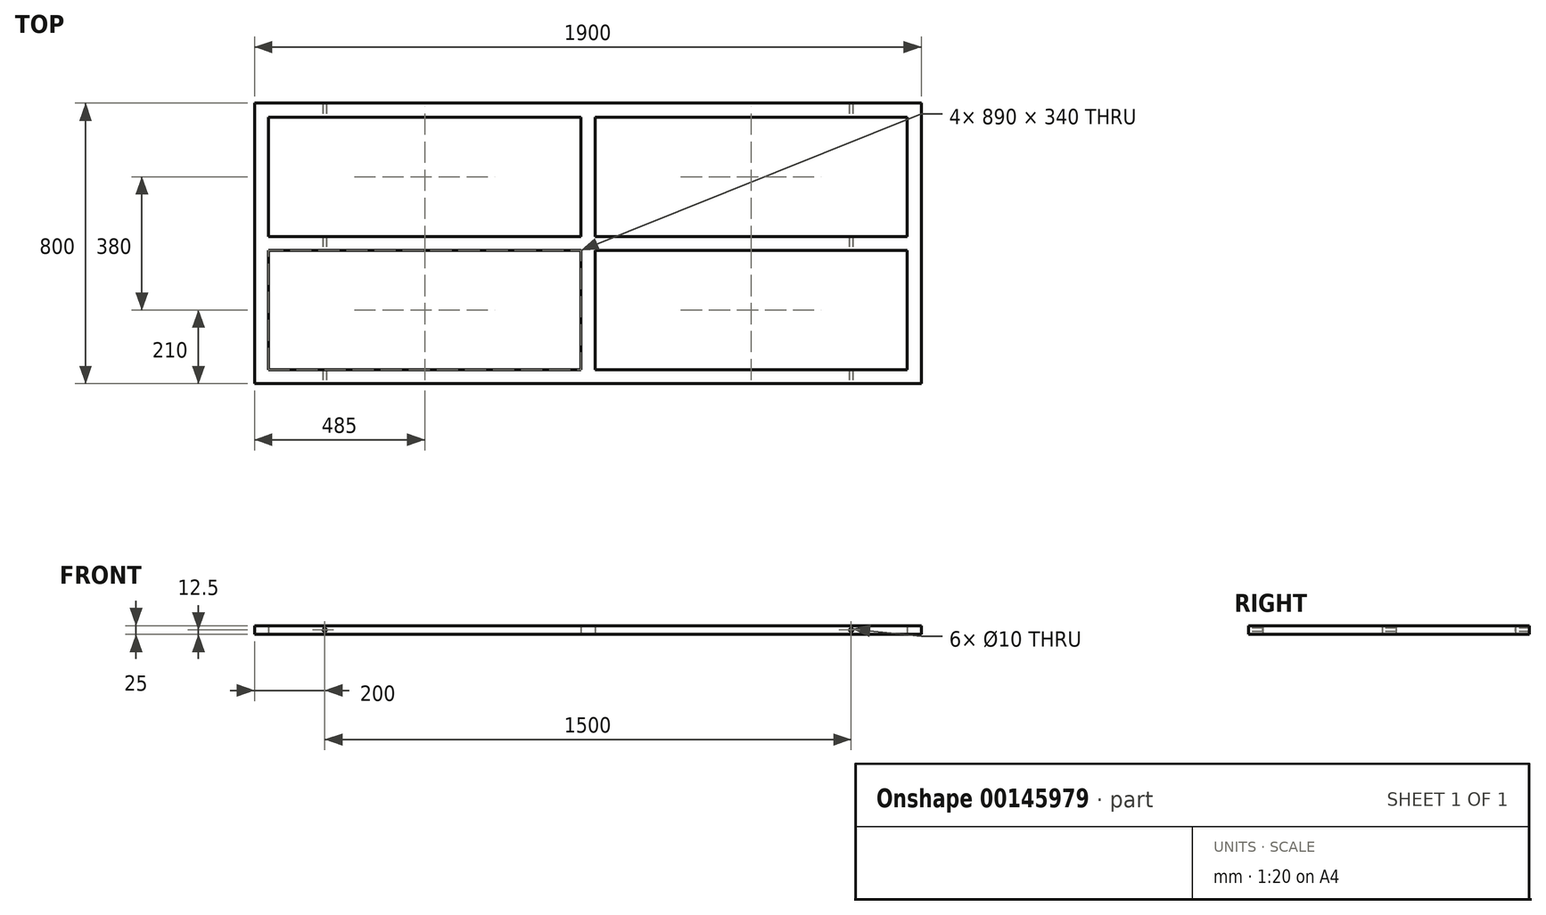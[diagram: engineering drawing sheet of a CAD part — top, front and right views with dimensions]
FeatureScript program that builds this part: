
annotation { "Feature Type Name" : "Feature", "Feature Type Description" : "" }
export const myFeature = defineFeature(function(context is Context, id is Id, definition is map)
    precondition{}
    {
        {
            var Q0;
            Q0=qCreatedBy(makeId("Top.planeOp"),FACE);
            var sketch = newSketch(context, id + "F0", { "sketchPlane" : qUnion([Q0])});
            skLineSegment(sketch, "E0.bottom", {"start": v(950, 400) * mm, "end": v(-950, 400) * mm});
            skLineSegment(sketch, "E0.top", {"start": v(950, -400) * mm, "end": v(-950, -400) * mm});
            skLineSegment(sketch, "E0.left", {"start": v(950, 400) * mm, "end": v(950, -400) * mm});
            skLineSegment(sketch, "E0.right", {"start": v(-950, 400) * mm, "end": v(-950, -400) * mm});
            skPoint(sketch, "E0.middle", {"position": v(0, 0) * mm});
            skLineSegment(sketch, "E1.bottom", {"start": v(910, 360) * mm, "end": v(-910, 360) * mm});
            skLineSegment(sketch, "E1.top", {"start": v(910, -360) * mm, "end": v(-910, -360) * mm});
            skLineSegment(sketch, "E1.left", {"start": v(910, 360) * mm, "end": v(910, -360) * mm});
            skLineSegment(sketch, "E1.right", {"start": v(-910, 360) * mm, "end": v(-910, -360) * mm});
            skLineSegment(sketch, "E2", {"start": v(0, -360) * mm, "end": v(0, 360) * mm, "construction": true});
            skLineSegment(sketch, "E3", {"start": v(0, 0) * mm, "end": v(-910, 0) * mm, "construction": true});
            skLineSegment(sketch, "E4", {"start": v(-910, -20) * mm, "end": v(-20, -20) * mm});
            skLineSegment(sketch, "E5", {"start": v(-910, 20) * mm, "end": v(-20, 20) * mm});
            skLineSegment(sketch, "E6", {"start": v(-20, -360) * mm, "end": v(-20, -20) * mm});
            skLineSegment(sketch, "E7", {"start": v(20, -360) * mm, "end": v(20, -20) * mm});
            skLineSegment(sketch, "E8.trimOffspring", {"start": v(20, -20) * mm, "end": v(910, -20) * mm});
            skLineSegment(sketch, "E9.trimOffspring", {"start": v(20, 20) * mm, "end": v(20, 360) * mm});
            skLineSegment(sketch, "E10.trimOffspring", {"start": v(20, 20) * mm, "end": v(910, 20) * mm});
            skLineSegment(sketch, "E11.trimOffspring", {"start": v(-20, 20) * mm, "end": v(-20, 360) * mm});
            skSolve(sketch);
        }
        {
            var Q0;
            Q0=makeQuery(id+"F0.imprint","IMPRINT",FACE,{"disambiguationData":[TD([[makeQuery(id+"F0.imprint","IMPRINT",EDGE,{"derivedFrom":sQuery(id+"F0.wireOp",EDGE,"E0.bottom")}),1.0]])]});
            var Q1;
            {var subQ3=sQuery(id+"F0.wireOp",EDGE,"E4");Q1=makeQuery(id+"F0.imprint","IMPRINT",FACE,{"disambiguationData":[TD([[makeQuery(id+"F0.imprint","IMPRINT",EDGE,{"derivedFrom":subQ3}),1.0]])]});}
            extrude(context, id + "F1", {"entities" : qUnion([Q0, Q1]), "depth" : 25 * mm});
        }
        {
            var Q0;
            Q0=makeQuery(id+"F1.opExtrude","SWEPT_FACE",FACE,{"disambiguationData":[OSD([sQuery(id+"F0.wireOp",EDGE,"E0.top")])]});
            var sketch = newSketch(context, id + "F2", { "sketchPlane" : qUnion([Q0])});
            skCircle(sketch, "E12", {"center": v(750, 12.5) * mm, "radius": 5 * mm});
            skPoint(sketch, "E12.centerSnap0", {"position": v(-950, 12.5) * mm});
            skCircle(sketch, "E13", {"center": v(-750, 12.5) * mm, "radius": 5 * mm});
            skPoint(sketch, "E13.centerSnap0", {"position": v(950, 12.5) * mm});
            skSolve(sketch);
        }
        {
            var Q0;
            Q0=makeQuery(id+"F2.imprint","IMPRINT",FACE,{"disambiguationData":[TD([[makeQuery(id+"F2.imprint","IMPRINT",EDGE,{"derivedFrom":sQuery(id+"F2.wireOp",EDGE,"E12")}),1.0]])]});
            var Q1;
            Q1=makeQuery(id+"F2.imprint","IMPRINT",FACE,{"disambiguationData":[TD([[makeQuery(id+"F2.imprint","IMPRINT",EDGE,{"derivedFrom":sQuery(id+"F2.wireOp",EDGE,"E13")}),1.0]])]});
            extrude(context, id + "F3", {"entities" : qUnion([Q0, Q1]), "operationType" : NewBodyOperationType.REMOVE, "endBound" : BoundingType.THROUGH_ALL, "oppositeDirection" : true, "depth" : 25 * mm});
        }
    });
